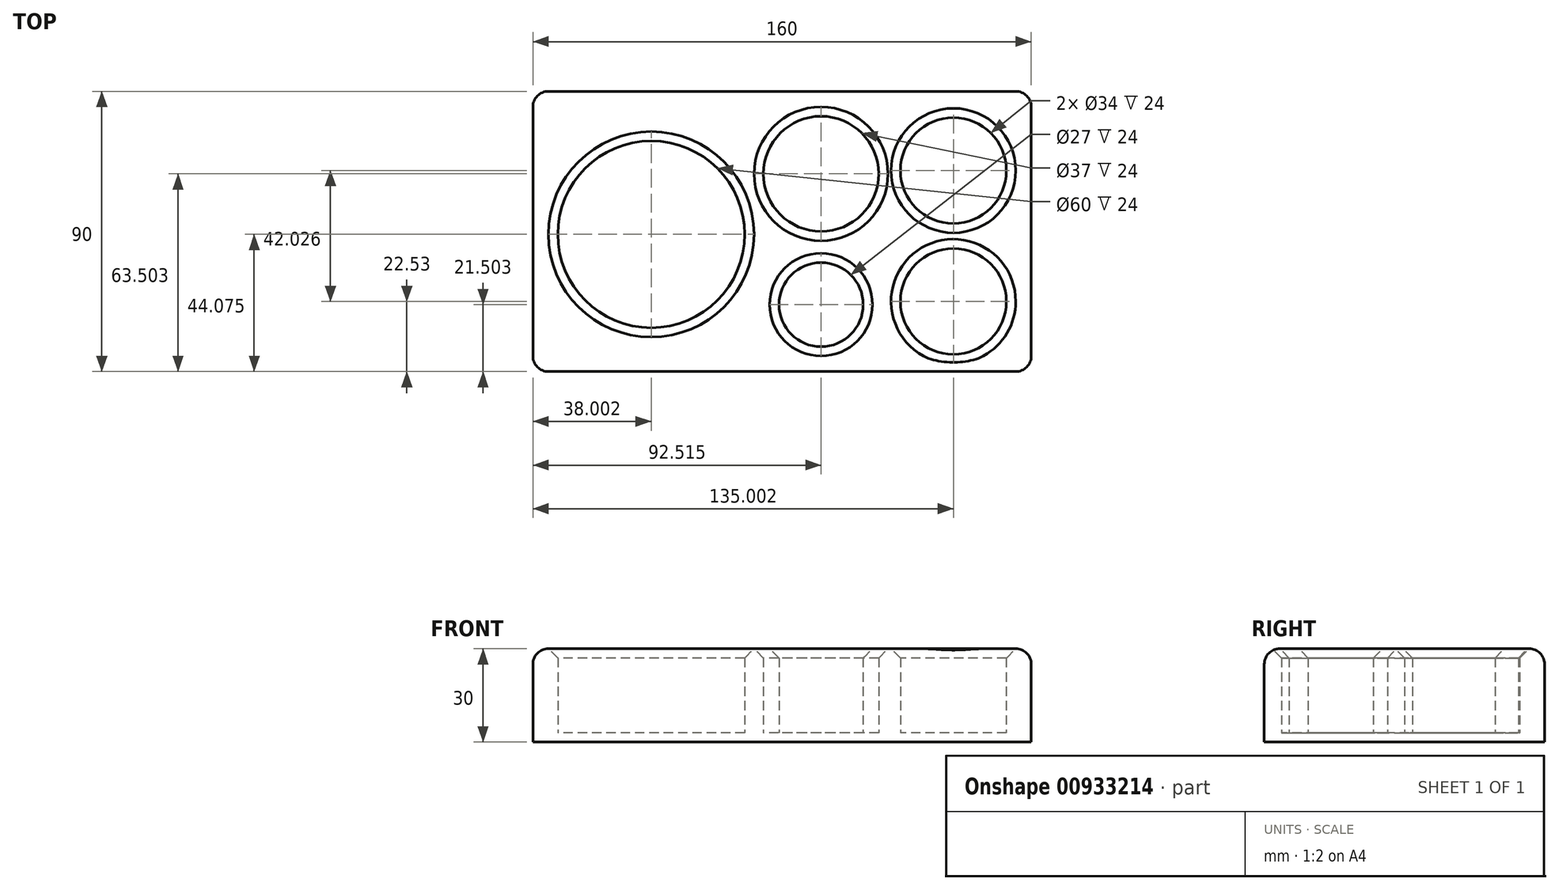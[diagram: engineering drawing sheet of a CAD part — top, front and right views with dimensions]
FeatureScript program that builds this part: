
annotation { "Feature Type Name" : "Feature", "Feature Type Description" : "" }
export const myFeature = defineFeature(function(context is Context, id is Id, definition is map)
    precondition{}
    {
        {
            var Q0;
            Q0=qCreatedBy(makeId("Top.planeOp"),FACE);
            var sketch = newSketch(context, id + "F0", { "sketchPlane" : qUnion([Q0])});
            skCircle(sketch, "E0", {"center": v(2.82, 35.9) * mm, "radius": 17 * mm});
            skLineSegment(sketch, "E1", {"start": v(2.82, 35.9) * mm, "end": v(2.82, -48.15) * mm, "construction": true});
            skCircle(sketch, "E2", {"center": v(2.82, -6.12) * mm, "radius": 17 * mm});
            skCircle(sketch, "E3", {"center": v(-39.67, -7.15) * mm, "radius": 13.5 * mm});
            skCircle(sketch, "E4", {"center": v(-39.67, 34.85) * mm, "radius": 18.5 * mm});
            skCircle(sketch, "E5", {"center": v(-94.18, 15.43) * mm, "radius": 30 * mm});
            skLineSegment(sketch, "E6.bottom", {"start": v(-132.18, 61.35) * mm, "end": v(27.82, 61.35) * mm});
            skLineSegment(sketch, "E6.top", {"start": v(-132.18, -28.65) * mm, "end": v(27.82, -28.65) * mm});
            skLineSegment(sketch, "E6.left", {"start": v(-132.18, 61.35) * mm, "end": v(-132.18, -28.65) * mm});
            skLineSegment(sketch, "E6.right", {"start": v(27.82, 61.35) * mm, "end": v(27.82, -28.65) * mm});
            skLineSegment(sketch, "E7", {"start": v(-39.67, 34.85) * mm, "end": v(-39.67, -28.65) * mm, "construction": true});
            skSolve(sketch);
        }
        {
            var Q0;
            Q0=makeQuery(id+"F0.imprint","IMPRINT",FACE,{"disambiguationData":[TD([[makeQuery(id+"F0.imprint","IMPRINT",EDGE,{"derivedFrom":sQuery(id+"F0.wireOp",EDGE,"E0")}),-1.0]])]});
            extrude(context, id + "F1", {"entities" : qUnion([Q0]), "depth" : 30 * mm, "offsetDistance" : 25 * mm});
        }
        {
            var Q0;
            Q0=makeQuery(id+"F0.imprint","IMPRINT",FACE,{"disambiguationData":[TD([[makeQuery(id+"F0.imprint","IMPRINT",EDGE,{"derivedFrom":sQuery(id+"F0.wireOp",EDGE,"E0")}),-1.0]])]});
            var Q1;
            Q1=makeQuery(id+"F0.imprint","IMPRINT",FACE,{"disambiguationData":[TD([[makeQuery(id+"F0.imprint","IMPRINT",EDGE,{"derivedFrom":sQuery(id+"F0.wireOp",EDGE,"E5")}),1.0]])]});
            var Q2;
            Q2=makeQuery(id+"F0.imprint","IMPRINT",FACE,{"disambiguationData":[TD([[makeQuery(id+"F0.imprint","IMPRINT",EDGE,{"derivedFrom":sQuery(id+"F0.wireOp",EDGE,"E3")}),1.0]])]});
            var Q3;
            Q3=makeQuery(id+"F0.imprint","IMPRINT",FACE,{"disambiguationData":[TD([[makeQuery(id+"F0.imprint","IMPRINT",EDGE,{"derivedFrom":sQuery(id+"F0.wireOp",EDGE,"E2")}),1.0]])]});
            var Q4;
            Q4=makeQuery(id+"F0.imprint","IMPRINT",FACE,{"disambiguationData":[TD([[makeQuery(id+"F0.imprint","IMPRINT",EDGE,{"derivedFrom":sQuery(id+"F0.wireOp",EDGE,"E0")}),1.0]])]});
            var Q5;
            Q5=makeQuery(id+"F0.imprint","IMPRINT",FACE,{"disambiguationData":[TD([[makeQuery(id+"F0.imprint","IMPRINT",EDGE,{"derivedFrom":sQuery(id+"F0.wireOp",EDGE,"E4")}),1.0]])]});
            extrude(context, id + "F2", {"entities" : qUnion([Q0, Q1, Q2, Q3, Q4, Q5]), "operationType" : NewBodyOperationType.ADD, "depth" : 3 * mm, "offsetDistance" : 25 * mm});
        }
        {
            var Q0;
            Q0=makeQuery(id+"F1.opExtrude","SWEPT_EDGE",EDGE,{"disambiguationData":[OSD([sQuery(id+"F0.wireOp",EDGE,"E6.bottom"),sQuery(id+"F0.wireOp",EDGE,"E6.right")])]});
            var Q1;
            Q1=makeQuery(id+"F1.opExtrude","SWEPT_EDGE",EDGE,{"disambiguationData":[OSD([sQuery(id+"F0.wireOp",EDGE,"E6.top"),sQuery(id+"F0.wireOp",EDGE,"E6.right")])]});
            var Q2;
            Q2=makeQuery(id+"F1.opExtrude","SWEPT_EDGE",EDGE,{"disambiguationData":[OSD([sQuery(id+"F0.wireOp",EDGE,"E6.top"),sQuery(id+"F0.wireOp",EDGE,"E6.left")])]});
            var Q3;
            Q3=makeQuery(id+"F1.opExtrude","SWEPT_EDGE",EDGE,{"disambiguationData":[OSD([sQuery(id+"F0.wireOp",EDGE,"E6.bottom"),sQuery(id+"F0.wireOp",EDGE,"E6.left")])]});
            fillet(context, id + "F3", {"entities" : qUnion([Q0, Q1, Q2, Q3]), "radius" : 5 * mm, "tangentPropagation" : true, "allowEdgeOverflow" : false});
        }
        {
            var Q0;
            Q0=makeQuery(id+"F1.opExtrude","CAP_EDGE",EDGE,{"disambiguationData":[OSD([sQuery(id+"F0.wireOp",EDGE,"E6.bottom")])],"isStart":false});
            var Q1;
            Q1=makeQuery(id+"F1.opExtrude","CAP_EDGE",EDGE,{"disambiguationData":[OSD([sQuery(id+"F0.wireOp",EDGE,"E6.right")])],"isStart":false});
            var Q2;
            Q2=makeQuery(id+"F1.opExtrude","CAP_EDGE",EDGE,{"disambiguationData":[OSD([sQuery(id+"F0.wireOp",EDGE,"E6.top")])],"isStart":false});
            var Q3;
            Q3=makeQuery(id+"F1.opExtrude","CAP_EDGE",EDGE,{"disambiguationData":[OSD([sQuery(id+"F0.wireOp",EDGE,"E6.left")])],"isStart":false});
            fillet(context, id + "F4", {"entities" : qUnion([Q0, Q1, Q2, Q3]), "radius" : 5 * mm, "tangentPropagation" : true, "allowEdgeOverflow" : false});
        }
        {
            var Q0;
            Q0=makeQuery(id+"F1.opExtrude","CAP_EDGE",EDGE,{"disambiguationData":[OSD([sQuery(id+"F0.wireOp",EDGE,"E5")])],"isStart":false});
            var Q1;
            Q1=makeQuery(id+"F1.opExtrude","CAP_EDGE",EDGE,{"disambiguationData":[OSD([sQuery(id+"F0.wireOp",EDGE,"E4")])],"isStart":false});
            var Q2;
            Q2=makeQuery(id+"F1.opExtrude","CAP_EDGE",EDGE,{"disambiguationData":[OSD([sQuery(id+"F0.wireOp",EDGE,"E0")])],"isStart":false});
            var Q3;
            Q3=makeQuery(id+"F1.opExtrude","CAP_EDGE",EDGE,{"disambiguationData":[OSD([sQuery(id+"F0.wireOp",EDGE,"E2")])],"isStart":false});
            var Q4;
            Q4=makeQuery(id+"F1.opExtrude","CAP_EDGE",EDGE,{"disambiguationData":[OSD([sQuery(id+"F0.wireOp",EDGE,"E3")])],"isStart":false});
            chamfer(context, id + "F5", {"entities" : qUnion([Q0, Q1, Q2, Q3, Q4]), "width" : 3 * mm, "tangentPropagation" : true});
        }
    });
